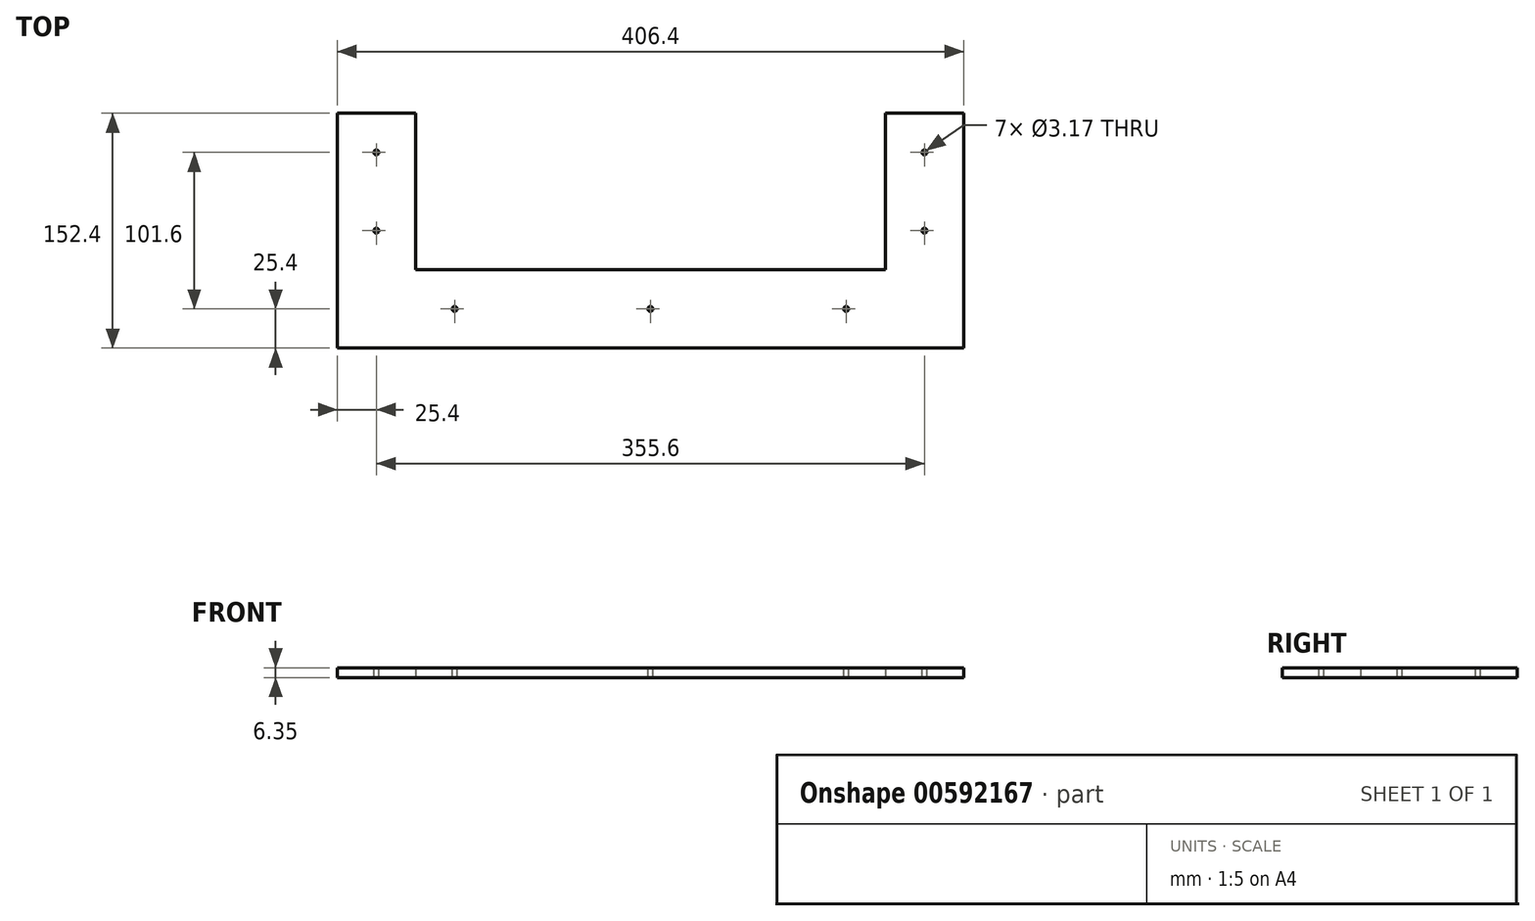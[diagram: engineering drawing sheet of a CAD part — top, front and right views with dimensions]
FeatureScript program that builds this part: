
annotation { "Feature Type Name" : "Feature", "Feature Type Description" : "" }
export const myFeature = defineFeature(function(context is Context, id is Id, definition is map)
    precondition{}
    {
        {
            var Q0;
            Q0=qCreatedBy(makeId("Top.planeOp"),FACE);
            var sketch = newSketch(context, id + "F0", { "sketchPlane" : qUnion([Q0])});
            skLineSegment(sketch, "E0.bottom", {"start": v(203.2, 76.2) * mm, "end": v(-203.2, 76.2) * mm});
            skLineSegment(sketch, "E0.top", {"start": v(203.2, -76.2) * mm, "end": v(-203.2, -76.2) * mm});
            skLineSegment(sketch, "E0.left", {"start": v(203.2, 76.2) * mm, "end": v(203.2, -76.2) * mm});
            skLineSegment(sketch, "E0.right", {"start": v(-203.2, 76.2) * mm, "end": v(-203.2, -76.2) * mm});
            skPoint(sketch, "E0.middle", {"position": v(0, 0) * mm});
            skLineSegment(sketch, "E1", {"start": v(-152.4, 76.2) * mm, "end": v(-152.4, -25.4) * mm});
            skLineSegment(sketch, "E2", {"start": v(-152.4, -25.4) * mm, "end": v(152.4, -25.4) * mm});
            skLineSegment(sketch, "E3", {"start": v(152.4, -25.4) * mm, "end": v(152.4, 76.2) * mm});
            skSolve(sketch);
        }
        {
            var Q0;
            Q0=makeQuery(id+"F0.imprint","IMPRINT",FACE,{"disambiguationData":[TD([[makeQuery(id+"F0.imprint","IMPRINT",EDGE,{"derivedFrom":sQuery(id+"F0.wireOp",EDGE,"E0.top")}),-1.0]])]});
            extrude(context, id + "F1", {"entities" : qUnion([Q0]), "depth" : 6.35 * mm, "offsetDistance" : 25.4 * mm});
        }
        {
            var Q0;
            Q0=makeQuery(id+"F1.opExtrude","CAP_FACE",FACE,{"disambiguationData":[OSD([sQuery(id+"F0.wireOp",EDGE,"E0.bottom"),sQuery(id+"F0.wireOp",EDGE,"E0.top"),sQuery(id+"F0.wireOp",EDGE,"E0.left"),sQuery(id+"F0.wireOp",EDGE,"E0.right"),sQuery(id+"F0.wireOp",EDGE,"E1"),sQuery(id+"F0.wireOp",EDGE,"E2"),sQuery(id+"F0.wireOp",EDGE,"E3")])],"isStart":false});
            var sketch = newSketch(context, id + "F2", { "sketchPlane" : qUnion([Q0])});
            skLineSegment(sketch, "E4", {"start": v(-177.8, 76.2) * mm, "end": v(-177.8, -76.2) * mm});
            skLineSegment(sketch, "E5", {"start": v(177.8, 76.2) * mm, "end": v(177.8, -76.2) * mm});
            skLineSegment(sketch, "E6", {"start": v(-203.2, -50.8) * mm, "end": v(203.2, -50.8) * mm});
            skCircle(sketch, "E7", {"center": v(-177.8, 50.8) * mm, "radius": 1.59 * mm});
            skCircle(sketch, "E8", {"center": v(-177.8, 0) * mm, "radius": 1.59 * mm});
            skCircle(sketch, "E9", {"center": v(177.8, 50.8) * mm, "radius": 1.59 * mm});
            skCircle(sketch, "E10", {"center": v(177.8, 0) * mm, "radius": 1.59 * mm});
            skCircle(sketch, "E11", {"center": v(-127, -50.8) * mm, "radius": 1.59 * mm});
            skCircle(sketch, "E12", {"center": v(127, -50.8) * mm, "radius": 1.59 * mm});
            skCircle(sketch, "E13", {"center": v(0, -50.8) * mm, "radius": 1.59 * mm});
            skSolve(sketch);
        }
        {
            var Q0;
            Q0 = qSketchRegion(id + "F2", true);
            extrude(context, id + "F3", {"entities" : qUnion([Q0]), "operationType" : NewBodyOperationType.REMOVE, "oppositeDirection" : true, "depth" : 25.4 * mm, "offsetDistance" : 25.4 * mm});
        }
    });
